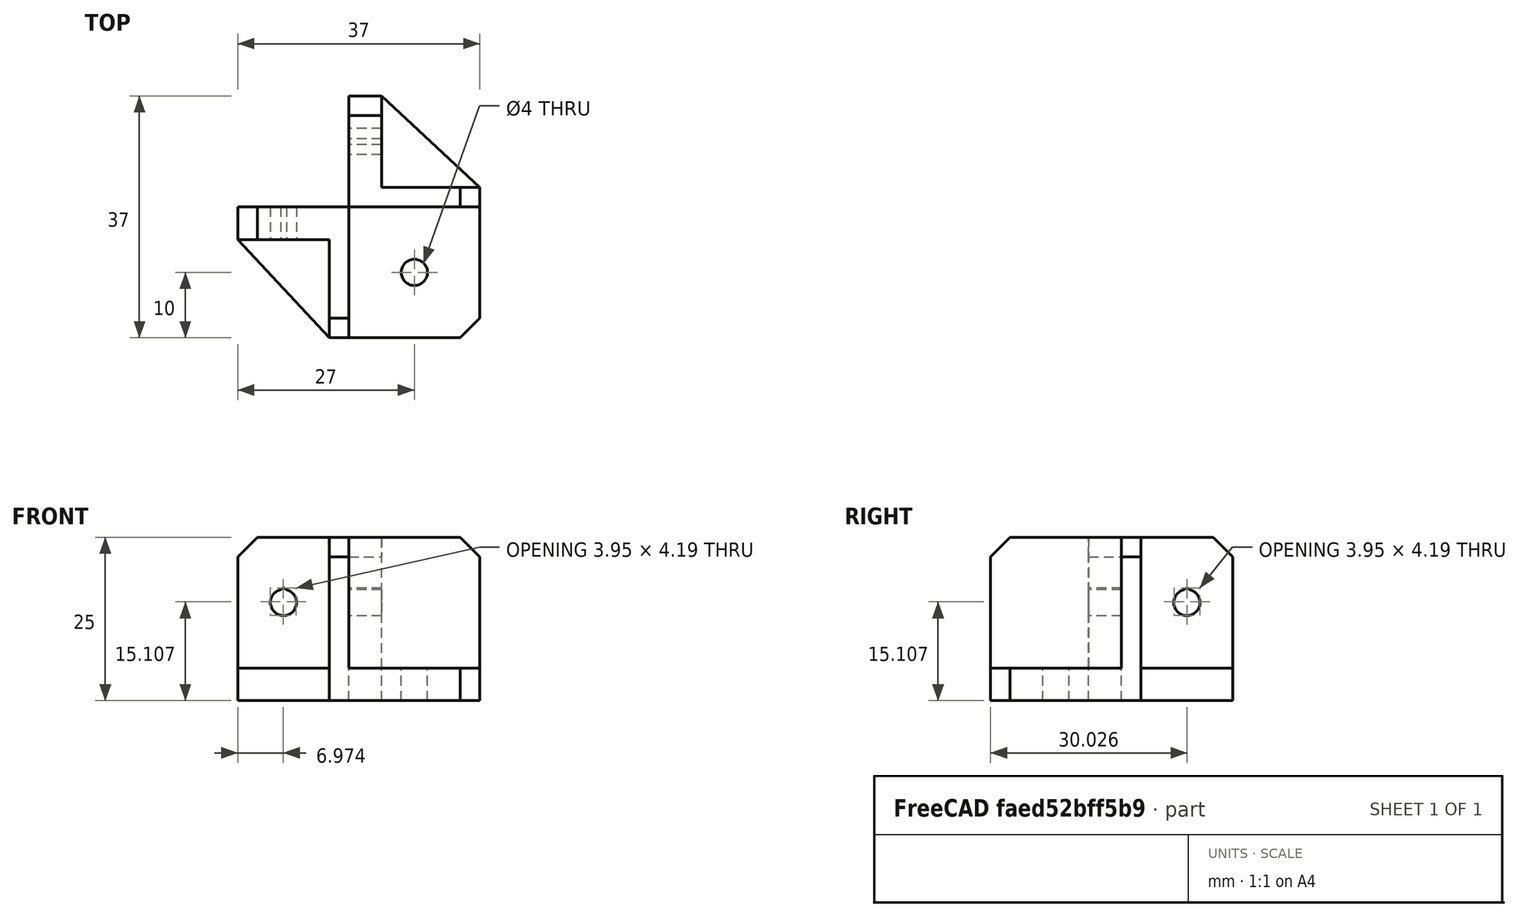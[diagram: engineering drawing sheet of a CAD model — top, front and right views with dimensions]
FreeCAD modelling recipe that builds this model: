
FCSTD DOCUMENT  (FreeCAD 0.18R14555 (Git shallow))
Label: filament-dryer-heated-bed-mounter
License: All rights reserved
LicenseURL: http://en.wikipedia.org/wiki/All_rights_reserved
objects: Part::Box×7, Part::Chamfer×7, Part::Cylinder×5, Part::Cut×5, Part::MultiFuse×1
note: 25 computed .brp shape members not serialized (recipe doc carries the construction recipe); baked Part::Feature solids carry a one-line shape summary decoded from their .brp

FEATURE [Part::Box] Box  label="Cube"
  AttacherType = Attacher::AttachEngine3D
  Height = 25
  Length = 20
  Width = 3
FEATURE [Part::Box] Box001  label="Cube001"
  AttacherType = Attacher::AttachEngine3D
  Height = 25
  Length = 5
  Width = 17
FEATURE [Part::Box] Box002  label="Cube002"
  AttacherType = Attacher::AttachEngine3D
  Height = 25
  Length = 17
  Placement = pos=(-17,-5,0) rot=(0,0,1;0rad)
  Width = 5
FEATURE [Part::Box] Box003  label="Cube003"
  AttacherType = Attacher::AttachEngine3D
  Height = 25
  Length = 3
  Placement = pos=(-3,-20,0) rot=(0,0,1;0rad)
  Width = 20
FEATURE [Part::Box] Box004  label="Cube004"
  AttacherType = Attacher::AttachEngine3D
  Height = 5
  Length = 20
  Placement = pos=(0,-20,0) rot=(0,0,1;0rad)
  Width = 20
FEATURE [Part::Chamfer] Chamfer
  Base = -> Box004
  Edges = 1 edges r=3: [Edge5]
FEATURE [Part::Chamfer] Chamfer003
  Base = -> Box
  Edges = 1 edges r=3: [Edge6]
FEATURE [Part::Chamfer] Chamfer004
  Base = -> Box003
  Edges = 1 edges r=3: [Edge10]
FEATURE [Part::Cylinder] Cylinder
  Angle = 360
  AttacherType = Attacher::AttachEngine3D
  Height = 10
  Placement = pos=(10,-10,0) rot=(0,0,1;0rad)
  Radius = 2
FEATURE [Part::Cut] Cut
  Base = -> Chamfer
  Tool = -> Cylinder
FEATURE [Part::Box] Box005  label="Cube005"
  AttacherType = Attacher::AttachEngine3D
  Height = 5
  Length = 17
  Placement = pos=(-17,-20,0) rot=(0,0,1;0rad)
  Width = 20
FEATURE [Part::Box] Box006  label="Cube006"
  AttacherType = Attacher::AttachEngine3D
  Height = 5
  Length = 20
  Width = 17
FEATURE [Part::Chamfer] Chamfer005
  Base = -> Box005
  Edges = 1 edges: [Edge1 r1=15 r2=14]
FEATURE [Part::Chamfer] Chamfer006
  Base = -> Box006
  Edges = 1 edges: [Edge7 r1=14 r2=15]
FEATURE [Part::Cylinder] Cylinder001
  Angle = 360
  AttacherType = Attacher::AttachEngine3D
  Height = 10
  Placement = pos=(10,10,16.7) rot=(-0.57735,-0.57735,0.57735;2.0944rad)
  Radius = 0.5
FEATURE [Part::Cylinder] Cylinder002
  Angle = 360
  AttacherType = Attacher::AttachEngine3D
  Height = 10
  Placement = pos=(-10,5,16.7) rot=(0,-0.707107,0.707107;3.14159rad)
  Radius = 0.5
FEATURE [Part::Cylinder] Cylinder003
  Angle = 360
  AttacherType = Attacher::AttachEngine3D
  Height = 10
  Placement = pos=(10,10,15) rot=(0.57735,0.57735,-0.57735;4.18879rad)
  Radius = 2
FEATURE [Part::Cylinder] Cylinder004
  Angle = 360
  AttacherType = Attacher::AttachEngine3D
  Height = 10
  Placement = pos=(-10,5,15) rot=(0,0.707107,-0.707107;3.14159rad)
  Radius = 2
FEATURE [Part::Cut] Cut001
  Base = -> Box002
  Tool = -> Cylinder004
FEATURE [Part::Cut] Cut002
  Base = -> Box001
  Tool = -> Cylinder003
FEATURE [Part::Chamfer] Chamfer007
  Base = -> Cut001
  Edges = 1 edges r=3: [Edge2]
FEATURE [Part::Chamfer] Chamfer008
  Base = -> Cut002
  Edges = 1 edges r=3: [Edge9]
FEATURE [Part::Cut] Cut003
  Base = -> Chamfer008
  Tool = -> Cylinder001
FEATURE [Part::Cut] Cut004
  Base = -> Chamfer007
  Tool = -> Cylinder002
FEATURE [Part::MultiFuse] Fusion
  Shapes = -> [Cut004,Cut003,Chamfer005,Chamfer004,Cut,Chamfer006,Chamfer003]
